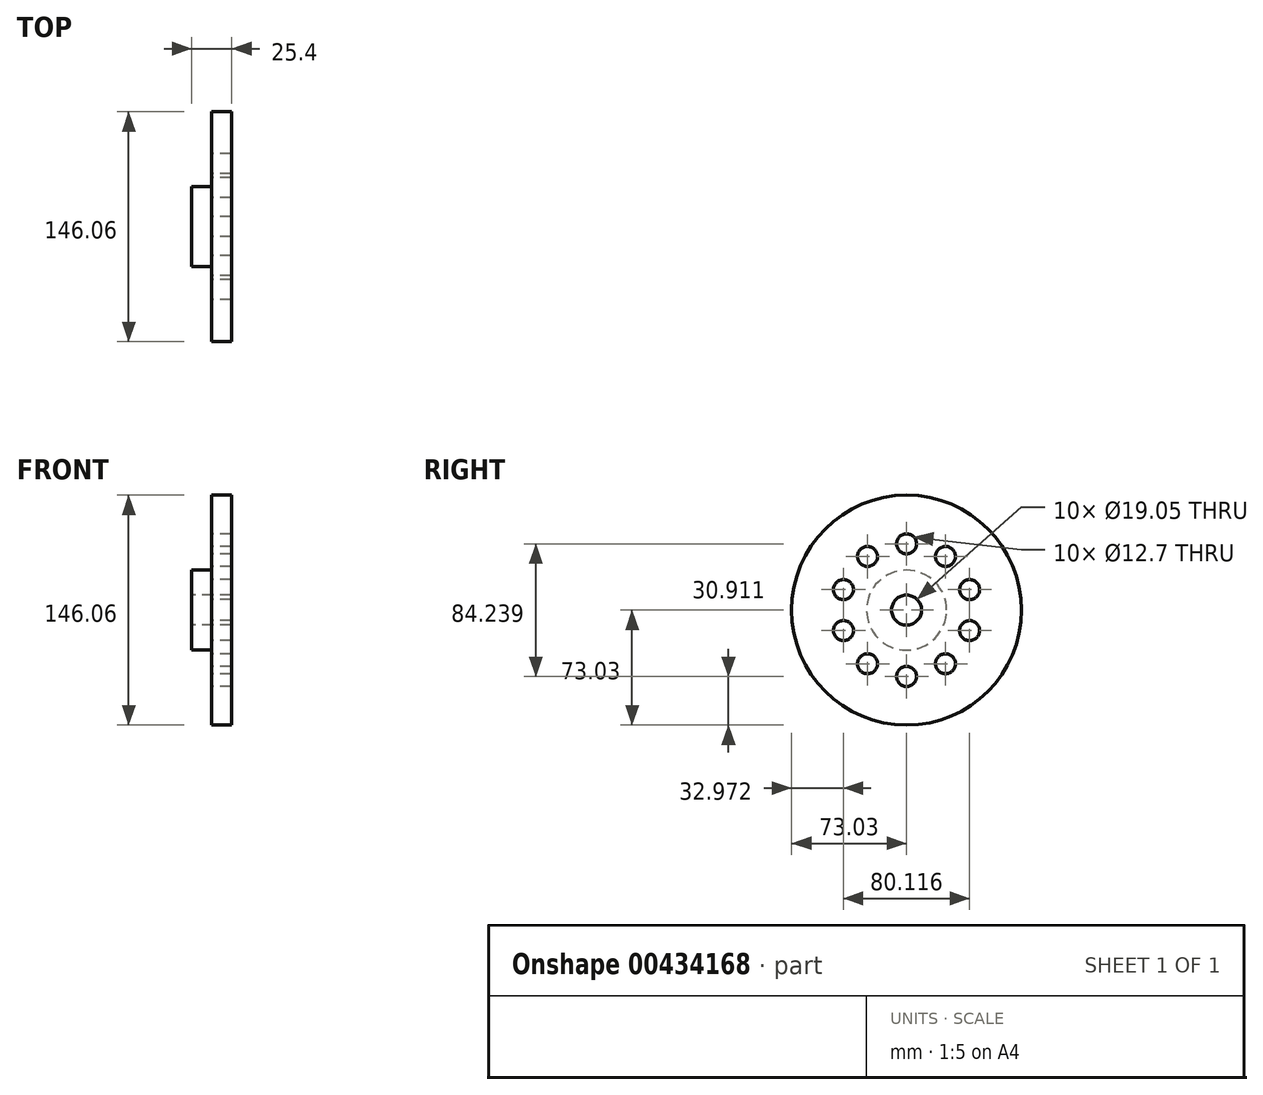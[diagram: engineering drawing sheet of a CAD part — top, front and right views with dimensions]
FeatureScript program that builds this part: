
annotation { "Feature Type Name" : "Feature", "Feature Type Description" : "" }
export const myFeature = defineFeature(function(context is Context, id is Id, definition is map)
    precondition{}
    {
        {
            var Q0;
            Q0=qCreatedBy(makeId("Front.planeOp"),FACE);
            var sketch = newSketch(context, id + "F0", { "sketchPlane" : qUnion([Q0])});
            skLineSegment(sketch, "E0.bottom", {"start": v(0, 0) * mm, "end": v(25.4, 0) * mm});
            skLineSegment(sketch, "E0.top", {"start": v(0, 9.52) * mm, "end": v(25.4, 9.52) * mm});
            skLineSegment(sketch, "E0.left", {"start": v(0, 0) * mm, "end": v(0, 9.52) * mm});
            skLineSegment(sketch, "E0.right", {"start": v(25.4, 0) * mm, "end": v(25.4, 9.52) * mm});
            skLineSegment(sketch, "E1", {"start": v(0, 9.52) * mm, "end": v(0, 25.4) * mm});
            skLineSegment(sketch, "E2", {"start": v(0, 25.4) * mm, "end": v(12.7, 25.4) * mm});
            skLineSegment(sketch, "E3", {"start": v(12.7, 25.4) * mm, "end": v(12.7, 73.02) * mm});
            skLineSegment(sketch, "E4", {"start": v(12.7, 73.02) * mm, "end": v(25.4, 73.02) * mm});
            skLineSegment(sketch, "E5", {"start": v(25.4, 73.02) * mm, "end": v(25.4, 9.52) * mm});
            skLineSegment(sketch, "E6", {"start": v(0, 0) * mm, "end": v(0, 5.1) * mm, "construction": true});
            skLineSegment(sketch, "E7", {"start": v(0, 9.52) * mm, "end": v(0, 0) * mm, "construction": true});
            skLineSegment(sketch, "E8", {"start": v(25.4, 0) * mm, "end": v(25.4, 9.52) * mm, "construction": true});
            skSolve(sketch);
        }
        {
            var Q0;
            Q0=makeQuery(id+"F0.imprint","IMPRINT",FACE,{"disambiguationData":[TD([[makeQuery(id+"F0.imprint","IMPRINT",EDGE,{"derivedFrom":sQuery(id+"F0.wireOp",EDGE,"E0.top")}),1.0]])]});
            var Q1;
            Q1=sQuery(id+"F0.wireOp",EDGE,"E0.bottom");
            revolve(context, id + "F1", {"entities" : qUnion([Q0]), "axis" : qUnion([Q1]), "revolveType" : RevolveType.FULL});
        }
        {
            var Q0;
            Q0=qCreatedBy(makeId("Right.planeOp"),FACE);
            var sketch = newSketch(context, id + "F2", { "sketchPlane" : qUnion([Q0])});
            skLineSegment(sketch, "E9", {"start": v(0, 0) * mm, "end": v(17.5, 0) * mm, "construction": true});
            skLineSegment(sketch, "E10", {"start": v(17.5, 0) * mm, "end": v(17.5, 41.91) * mm});
            skPoint(sketch, "E11", {"position": v(0, 42.12) * mm});
            skSolve(sketch);
        }
        {
            var Q0;
            Q0=sQuery(id+"F2.wireOp",VERTEX,"E11");
            var Q1;
            Q1=makeQuery(id+"F1.opRevolve","SWEPT_BODY",BODY,{"disambiguationData":[OSD([sQuery(id+"F0.wireOp",EDGE,"E0.top"),sQuery(id+"F0.wireOp",EDGE,"E1"),sQuery(id+"F0.wireOp",EDGE,"E2"),sQuery(id+"F0.wireOp",EDGE,"E3"),sQuery(id+"F0.wireOp",EDGE,"E4"),sQuery(id+"F0.wireOp",EDGE,"E5")])]});
            hole(context, id + "F3", {"style" : HoleStyle.SIMPLE, "endStyle" : HoleEndStyle.THROUGH, "oppositeDirection" : true, "holeDiameter" : 12.7 * mm, "isTappedThrough" : true, "tappedDepth" : 12.7 * mm, "tapClearance" : 3, "locations" : qUnion([Q0]), "scope" : qUnion([Q1])});
        }
        {
            var Q0;
            Q0=makeQuery(id+"F1.opRevolve","SWEPT_BODY",BODY,{"disambiguationData":[OSD([sQuery(id+"F0.wireOp",EDGE,"E0.top"),sQuery(id+"F0.wireOp",EDGE,"E1"),sQuery(id+"F0.wireOp",EDGE,"E2"),sQuery(id+"F0.wireOp",EDGE,"E3"),sQuery(id+"F0.wireOp",EDGE,"E4"),sQuery(id+"F0.wireOp",EDGE,"E5")])]});
            var Q1;
            Q1=makeQuery(id+"F1.opRevolve","SWEPT_EDGE",EDGE,{"disambiguationData":[OSD([sQuery(id+"F0.wireOp",EDGE,"E0.top"),sQuery(id+"F0.wireOp",EDGE,"E0.left"),sQuery(id+"F0.wireOp",EDGE,"E1")])]});
            circularPattern(context, id + "F4", {"entities" : qUnion([Q0]), "axis" : qUnion([Q1]), "angle" : 360 * degree, "instanceCount" : 10, "equalSpace" : true});
        }
    });
